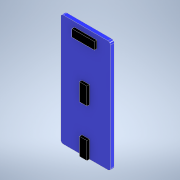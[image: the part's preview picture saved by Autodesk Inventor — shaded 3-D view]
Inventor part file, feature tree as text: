
AUTODESK INVENTOR PART (.ipt)
format: ipt  version: 2021 (Build 250183000, 183)  size: 168,960 bytes
history: native  units: mm
features: extrude x3, sketch x3, other x2, fillet x1
ambient origin geometry x8: Origin, YZ Plane, XZ Plane, XY Plane, X Axis, Y Axis, Z Axis, Center Point
bodies: Body1 (feature_tree), Body2 (feature_tree)
feature tree (9):
  other  "Sólido1"
  extrude  "Extrusão1"  Depth=45.0mm
  fillet  "Arredondamento1"  Radius=1.5mm
  extrude  "Extrusão2"  Depth=3.0mm
  extrude  "Extrusão3"  Depth=3.0mm
  sketch  "Esboço1"  dims[d0=20.0mm d1=45.0mm d6=1.5mm d7=0.0mm]
  sketch  "Esboço2"  dims[d8=1.0mm d9=3.0mm]
  sketch  "Esboço3"  dims[d10=7.0mm d11=3.0mm d12=7.0mm d13=10.0mm d19=12.0mm d20=9.0mm d21=3.0mm d22=2.0mm d23=5.5mm d24=1.0mm d25=0.0mm d30=8.5mm d31=2.5mm d32=22.5mm d33=6.0mm d34=1.25mm d35=0.5mm d36=3.0mm d37=0.0mm]
  other  "Sólido2"
